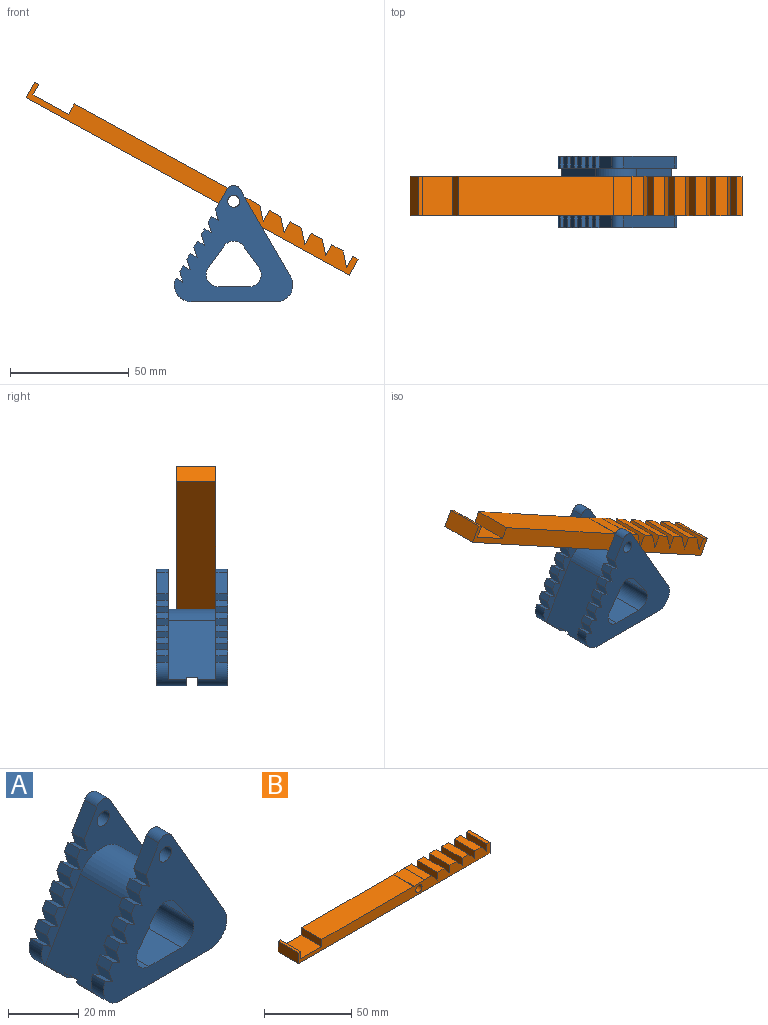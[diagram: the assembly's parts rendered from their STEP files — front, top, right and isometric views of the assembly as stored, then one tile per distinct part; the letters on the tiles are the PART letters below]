
ASSEMBLY  parts=2 mates=1
PART A: 64 faces, bbox 49.8x30x49 mm
  f0: plane 35.78x12.5mm, normal (0,0,-1), area 447.3mm2, adj f19,f58,f60,f61
  f1: plane 49.78x47.01mm, normal (0,1,0), area 480.9mm2, adj f3,f5,f7,f9,f11,f12,f13,f15
  f2: plane 5x2.51mm, normal (-0.87,0,0.5), area 14.5mm2, adj f19,f20,f49,f54
  f3: plane 5x2.51mm, normal (-0.87,0,0.5), area 14.5mm2, adj f1,f18,f52,f55
  f4: plane 5x2.51mm, normal (-0.87,0,0.5), area 14.5mm2, adj f19,f20,f45,f50
  f5: plane 5x2.51mm, normal (-0.87,0,0.5), area 14.5mm2, adj f1,f18,f48,f51
  f6: plane 5x2.51mm, normal (-0.87,0,0.5), area 14.5mm2, adj f19,f20,f41,f46
  f7: plane 5x2.51mm, normal (-0.87,0,0.5), area 14.5mm2, adj f1,f18,f44,f47
  f8: plane 5x2.51mm, normal (-0.87,0,0.5), area 14.5mm2, adj f19,f20,f37,f42
  f9: plane 5x2.51mm, normal (-0.87,0,0.5), area 14.5mm2, adj f1,f18,f40,f43
  f10: plane 5x2.51mm, normal (-0.87,0,0.5), area 14.5mm2, adj f19,f20,f33,f38
  f11: plane 5x2.51mm, normal (-0.87,0,0.5), area 14.5mm2, adj f1,f18,f36,f39
  f12: plane 24.59x20mm, normal (-0.87,0,0.5), area 563.4mm2, adj f1,f20,f24,f57,f58,f59,f61,f62
  f13: plane 25.35x20mm, normal (0.87,0,0.5), area 576.6mm2, adj f1,f20,f24,f57,f58,f59,f60,f63
  f14: plane 35.78x12.5mm, normal (0,0,-1), area 447.3mm2, adj f18,f57,f62,f63
  f15: plane 36.96x21.34mm, normal (0.87,0,0.5), area 213.4mm2, adj f1,f18,f23,f63
  f16: plane 8.85x5.11mm, normal (-0.87,0,0.5), area 51.1mm2, adj f19,f20,f22,f53
  f17: plane 36.96x21.34mm, normal (0.87,0,0.5), area 213.4mm2, adj f19,f20,f22,f60
  f18: plane 49.78x48.96mm, normal (0,-1,0), area 1116mm2, adj f3,f5,f7,f9,f11,f14,f15,f21
  f19: plane 49.78x48.96mm, normal (0,1,0), area 1116mm2, adj f0,f2,f4,f6,f8,f10,f16,f17
  f20: plane 49.78x47.01mm, normal (0,-1,0), area 480.9mm2, adj f2,f4,f6,f8,f10,f12,f13,f16
  f21: plane 8.85x5.11mm, normal (-0.87,0,0.5), area 51.1mm2, adj f1,f18,f23,f56
  f22: cylinder r=3mm len=5.2mm, axis (0,1,0), area 31.4mm2, adj f16,f17,f19,f20
  f23: cylinder r=3mm len=5.2mm, axis (0,1,0), area 31.4mm2, adj f1,f15,f18,f21
  f24: cylinder r=10mm len=20mm, axis (0,1,0), area 418.9mm2, adj f1,f12,f13,f20
  f25: cylinder r=2.5mm len=5mm, axis (0,1,0), area 78.5mm2, adj f19,f20
  f26: cylinder r=2.5mm len=5mm, axis (0,1,0), area 78.5mm2, adj f1,f18
  f27: plane 30x9.24mm, normal (0.81,0,-0.58), area 340.5mm2, adj f18,f19,f30,f32
  f28: plane 30x13.18mm, normal (0,0,1), area 395.5mm2, adj f18,f19,f30,f31
  f29: plane 30x9.24mm, normal (-0.81,0,-0.58), area 340.5mm2, adj f18,f19,f31,f32
  f30: cylinder r=5mm len=30mm, axis (0,1,0), area 328.6mm2, adj f18,f19,f27,f28
  f31: cylinder r=5mm len=30mm, axis (0,1,0), area 328.6mm2, adj f18,f19,f28,f29
  f32: cylinder r=5mm len=30mm, axis (0,1,0), area 285.4mm2, adj f18,f19,f27,f29
  f33: plane 5x4.37mm, normal (-0.95,0,-0.3), area 22.9mm2, adj f10,f19,f20,f34
  f34: plane 5x2.92mm, normal (0.5,0,0.87), area 16.9mm2, adj f19,f20,f33,f61
  f35: plane 5x2.92mm, normal (0.5,0,0.87), area 16.9mm2, adj f1,f18,f36,f62
  f36: plane 5x4.37mm, normal (-0.95,0,-0.3), area 22.9mm2, adj f1,f11,f18,f35
  f37: plane 5x4.37mm, normal (-0.95,0,-0.3), area 22.9mm2, adj f8,f19,f20,f38
  f38: plane 5x2.92mm, normal (0.5,0,0.87), area 16.9mm2, adj f10,f19,f20,f37
  f39: plane 5x2.92mm, normal (0.5,0,0.87), area 16.9mm2, adj f1,f11,f18,f40
  f40: plane 5x4.37mm, normal (-0.95,0,-0.3), area 22.9mm2, adj f1,f9,f18,f39
  f41: plane 5x4.37mm, normal (-0.95,0,-0.3), area 22.9mm2, adj f6,f19,f20,f42
  f42: plane 5x2.92mm, normal (0.5,0,0.87), area 16.9mm2, adj f8,f19,f20,f41
  f43: plane 5x2.92mm, normal (0.5,0,0.87), area 16.9mm2, adj f1,f9,f18,f44
  f44: plane 5x4.37mm, normal (-0.95,0,-0.3), area 22.9mm2, adj f1,f7,f18,f43
  f45: plane 5x4.37mm, normal (-0.95,0,-0.3), area 22.9mm2, adj f4,f19,f20,f46
  f46: plane 5x2.92mm, normal (0.5,0,0.87), area 16.9mm2, adj f6,f19,f20,f45
  f47: plane 5x2.92mm, normal (0.5,0,0.87), area 16.9mm2, adj f1,f7,f18,f48
  f48: plane 5x4.37mm, normal (-0.95,0,-0.3), area 22.9mm2, adj f1,f5,f18,f47
  f49: plane 5x4.37mm, normal (-0.95,0,-0.3), area 22.9mm2, adj f2,f19,f20,f50
  f50: plane 5x2.92mm, normal (0.5,0,0.87), area 16.9mm2, adj f4,f19,f20,f49
  f51: plane 5x2.92mm, normal (0.5,0,0.87), area 16.9mm2, adj f1,f5,f18,f52
  f52: plane 5x4.37mm, normal (-0.95,0,-0.3), area 22.9mm2, adj f1,f3,f18,f51
  f53: plane 5x4.37mm, normal (-0.95,0,-0.3), area 22.9mm2, adj f16,f19,f20,f54
  f54: plane 5x2.92mm, normal (0.5,0,0.87), area 16.9mm2, adj f2,f19,f20,f53
  f55: plane 5x2.92mm, normal (0.5,0,0.87), area 16.9mm2, adj f1,f3,f18,f56
  f56: plane 5x4.37mm, normal (-0.95,0,-0.3), area 22.9mm2, adj f1,f18,f21,f55
  f57: plane 46.16x3.5mm, normal (0,1,0), area 153.2mm2, adj f12,f13,f14,f59,f62,f63
  f58: plane 46.16x3.5mm, normal (0,-1,0), area 153.2mm2, adj f0,f12,f13,f59,f60,f61
  f59: plane 44.8x5mm, normal (0,0,-1), area 224mm2, adj f12,f13,f57,f58
  f60: cylinder r=7mm len=12.5mm, axis (0,-1,0), area 113.4mm2, adj f0,f13,f17,f19,f20,f58
  f61: cylinder r=7mm len=12.5mm, axis (0,1,0), area 118mm2, adj f0,f12,f19,f20,f34,f58
  f62: cylinder r=7mm len=12.5mm, axis (0,1,0), area 118mm2, adj f1,f12,f14,f18,f35,f57
  f63: cylinder r=7mm len=12.5mm, axis (0,-1,0), area 113.4mm2, adj f1,f13,f14,f15,f18,f57
PART B: 30 faces, bbox 155x16.5x7.8 mm
  f0: plane 155x7.75mm, normal (0,1,0), area 1011.1mm2, adj f1,f2,f3,f4,f5,f6,f7,f8
  f1: plane 16.5x5.43mm, normal (0,0,1), area 89.6mm2, adj f0,f18,f27,f28
  f2: plane 16.5x5.43mm, normal (0,0,1), area 89.6mm2, adj f0,f18,f25,f26
  f3: plane 16.5x5.43mm, normal (0,0,1), area 89.6mm2, adj f0,f18,f23,f24
  f4: plane 16.5x5.43mm, normal (0,0,1), area 89.6mm2, adj f0,f18,f21,f22
  f5: plane 16.5x2.54mm, normal (0,0,1), area 41.8mm2, adj f0,f9,f18,f20
  f6: plane 16.5x8.58mm, normal (-0.02,0,1), area 141.7mm2, adj f0,f8,f18,f19
  f7: plane 74.4x16.5mm, normal (0,0,1), area 1227.6mm2, adj f0,f8,f16,f18
  f8: cylinder r=5mm len=16.5mm, axis (0,1,0), area 3.8mm2, adj f0,f6,f7,f18
  f9: plane 16.5x7.75mm, normal (1,0,0), area 127.9mm2, adj f0,f5,f11,f18
  f10: plane 16.5x5.7mm, normal (0,0,1), area 94mm2, adj f0,f18,f19,f29
  f11: plane 155x16.5mm, normal (0,0,-1), area 2557.5mm2, adj f0,f9,f12,f18
  f12: plane 16.5x7.5mm, normal (-1,0,0), area 123.7mm2, adj f0,f11,f13,f18
  f13: plane 16.5x1.98mm, normal (0,0,1), area 32.7mm2, adj f0,f12,f15,f18
  f14: cylinder r=2.5mm len=16.5mm, axis (0,-1,0), area 259.2mm2, adj f0,f18
  f15: plane 16.5x5mm, normal (1,0,0), area 82.5mm2, adj f0,f13,f17,f18
  f16: plane 16.5x5mm, normal (-1,0,0), area 82.5mm2, adj f0,f7,f17,f18
  f17: plane 17x16.5mm, normal (0,0,1), area 280.5mm2, adj f0,f15,f16,f18
  f18: plane 155x7.75mm, normal (0,-1,0), area 1011.1mm2, adj f1,f2,f3,f4,f5,f6,f7,f8
  f19: plane 16.5x0.05mm, normal (-1,0,0), area 0.8mm2, adj f0,f6,f10,f18
  f20: plane 16.5x5.33mm, normal (-1,0,0), area 87.9mm2, adj f0,f5,f18,f21
  f21: plane 16.5x5.33mm, normal (0.76,0,0.65), area 115.8mm2, adj f0,f4,f18,f20
  f22: plane 16.5x5.33mm, normal (-1,0,0), area 87.9mm2, adj f0,f4,f18,f23
  f23: plane 16.5x5.33mm, normal (0.76,0,0.65), area 115.8mm2, adj f0,f3,f18,f22
  f24: plane 16.5x5.33mm, normal (-1,0,0), area 87.9mm2, adj f0,f3,f18,f25
  f25: plane 16.5x5.33mm, normal (0.76,0,0.65), area 115.8mm2, adj f0,f2,f18,f24
  f26: plane 16.5x5.33mm, normal (-1,0,0), area 87.9mm2, adj f0,f2,f18,f27
  f27: plane 16.5x5.33mm, normal (0.76,0,0.65), area 115.8mm2, adj f0,f1,f18,f26
  f28: plane 16.5x5.33mm, normal (-1,0,0), area 87.9mm2, adj f0,f1,f18,f29
  f29: plane 16.5x5.33mm, normal (0.76,0,0.65), area 115.8mm2, adj f0,f10,f18,f28
PLACE A t=(2.98,17.66,-23.8)mm fixed
PLACE B rot(axis=(0,1,0),28.8deg) t=(7.74,10.66,18.2)mm
MATE revolute B.f14 <-> A.f25  axis (0,-1,0) through (5,-7.34,18.42)mm
